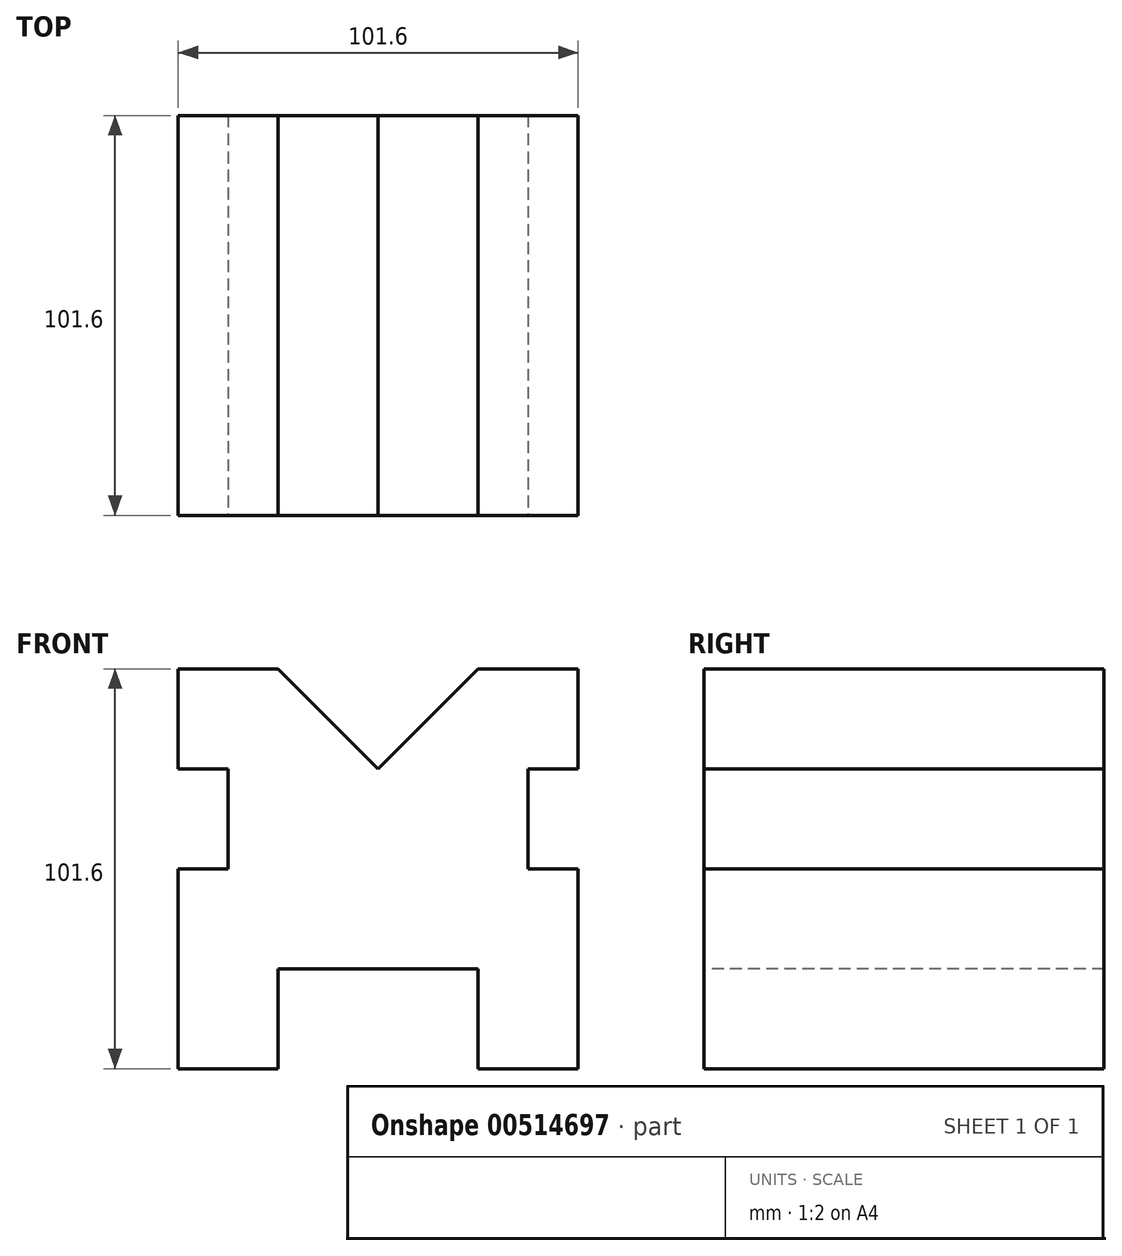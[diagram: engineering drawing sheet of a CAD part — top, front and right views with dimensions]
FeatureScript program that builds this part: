
annotation { "Feature Type Name" : "Feature", "Feature Type Description" : "" }
export const myFeature = defineFeature(function(context is Context, id is Id, definition is map)
    precondition{}
    {
        {
            var Q0;
            Q0=qCreatedBy(makeId("Front.planeOp"),FACE);
            var sketch = newSketch(context, id + "F0", { "sketchPlane" : qUnion([Q0])});
            skLineSegment(sketch, "E0", {"start": v(-48.51, 69.98) * mm, "end": v(-48.51, -31.62) * mm});
            skLineSegment(sketch, "E1", {"start": v(-48.51, 69.98) * mm, "end": v(53.09, 69.98) * mm});
            skLineSegment(sketch, "E2", {"start": v(53.09, 69.98) * mm, "end": v(53.09, -31.62) * mm});
            skLineSegment(sketch, "E3", {"start": v(-48.51, -31.62) * mm, "end": v(53.09, -31.62) * mm});
            skSolve(sketch);
        }
        {
            var Q0;
            Q0=makeQuery(id+"F0.imprint","IMPRINT",FACE,{"disambiguationData":[TD([[makeQuery(id+"F0.imprint","IMPRINT",EDGE,{"derivedFrom":sQuery(id+"F0.wireOp",EDGE,"E0")}),1.0]])]});
            extrude(context, id + "F1", {"entities" : qUnion([Q0]), "depth" : 101.6 * mm, "offsetDistance" : 25.4 * mm});
        }
        {
            var Q0;
            Q0=makeQuery(id+"F1.opExtrude","CAP_FACE",FACE,{"disambiguationData":[OSD([sQuery(id+"F0.wireOp",EDGE,"E0"),sQuery(id+"F0.wireOp",EDGE,"E1"),sQuery(id+"F0.wireOp",EDGE,"E2"),sQuery(id+"F0.wireOp",EDGE,"E3")])],"isStart":false});
            var sketch = newSketch(context, id + "F2", { "sketchPlane" : qUnion([Q0])});
            skLineSegment(sketch, "E4", {"start": v(-23.11, 69.98) * mm, "end": v(27.69, 69.98) * mm});
            skLineSegment(sketch, "E5", {"start": v(2.29, 44.58) * mm, "end": v(-23.11, 69.98) * mm});
            skLineSegment(sketch, "E6", {"start": v(2.29, 44.58) * mm, "end": v(27.69, 69.98) * mm});
            skSolve(sketch);
        }
        {
            var Q0;
            Q0 = qSketchRegion(id + "F2", true);
            extrude(context, id + "F3", {"entities" : qUnion([Q0]), "operationType" : NewBodyOperationType.REMOVE, "oppositeDirection" : true, "depth" : 101.6 * mm, "offsetDistance" : 25.4 * mm});
        }
        {
            var Q0;
            Q0=makeQuery(id+"F1.opExtrude","CAP_FACE",FACE,{"disambiguationData":[OSD([sQuery(id+"F0.wireOp",EDGE,"E0"),sQuery(id+"F0.wireOp",EDGE,"E1"),sQuery(id+"F0.wireOp",EDGE,"E2"),sQuery(id+"F0.wireOp",EDGE,"E3")])],"isStart":false});
            var sketch = newSketch(context, id + "F4", { "sketchPlane" : qUnion([Q0])});
            skLineSegment(sketch, "E7", {"start": v(-48.51, 44.58) * mm, "end": v(-48.51, 19.18) * mm});
            skLineSegment(sketch, "E8", {"start": v(-48.51, 19.18) * mm, "end": v(-35.81, 19.18) * mm});
            skLineSegment(sketch, "E9", {"start": v(-35.81, 19.18) * mm, "end": v(-35.81, 44.58) * mm});
            skLineSegment(sketch, "E10", {"start": v(-35.81, 44.58) * mm, "end": v(-48.51, 44.58) * mm});
            skLineSegment(sketch, "E11", {"start": v(53.09, 44.58) * mm, "end": v(40.39, 44.58) * mm});
            skLineSegment(sketch, "E12", {"start": v(40.39, 19.18) * mm, "end": v(53.09, 19.18) * mm});
            skLineSegment(sketch, "E13", {"start": v(40.39, 44.58) * mm, "end": v(40.39, 19.18) * mm});
            skSolve(sketch);
        }
        {
            var Q0;
            Q0 = qSketchRegion(id + "F4", true);
            var Q1;
            {var subQ0=sQuery(id+"F4.wireOp",EDGE,"E11");Q1=makeQuery(id+"F4.imprint","IMPRINT",FACE,{"disambiguationData":[TD([[makeQuery(id+"F4.imprint","IMPRINT",EDGE,{"derivedFrom":subQ0}),1.0]])]});}
            extrude(context, id + "F5", {"entities" : qUnion([Q0, Q1]), "operationType" : NewBodyOperationType.REMOVE, "oppositeDirection" : true, "depth" : 101.6 * mm, "offsetDistance" : 25.4 * mm});
        }
        {
            var Q0;
            Q0=makeQuery(id+"F1.opExtrude","CAP_FACE",FACE,{"disambiguationData":[OSD([sQuery(id+"F0.wireOp",EDGE,"E0"),sQuery(id+"F0.wireOp",EDGE,"E1"),sQuery(id+"F0.wireOp",EDGE,"E2"),sQuery(id+"F0.wireOp",EDGE,"E3")])],"isStart":false});
            var sketch = newSketch(context, id + "F6", { "sketchPlane" : qUnion([Q0])});
            skLineSegment(sketch, "E14.bottom", {"start": v(-23.11, -31.62) * mm, "end": v(27.69, -31.62) * mm});
            skLineSegment(sketch, "E14.top", {"start": v(-23.11, -6.22) * mm, "end": v(27.69, -6.22) * mm});
            skLineSegment(sketch, "E14.left", {"start": v(-23.11, -31.62) * mm, "end": v(-23.11, -6.22) * mm});
            skLineSegment(sketch, "E14.right", {"start": v(27.69, -31.62) * mm, "end": v(27.69, -6.22) * mm});
            skSolve(sketch);
        }
        {
            var Q0;
            Q0=makeQuery(id+"F6.imprint","IMPRINT",FACE,{"disambiguationData":[TD([[makeQuery(id+"F6.imprint","IMPRINT",EDGE,{"derivedFrom":sQuery(id+"F6.wireOp",EDGE,"E14.bottom")}),1.0]])]});
            extrude(context, id + "F7", {"entities" : qUnion([Q0]), "operationType" : NewBodyOperationType.REMOVE, "oppositeDirection" : true, "depth" : 101.6 * mm, "offsetDistance" : 25.4 * mm});
        }
    });
